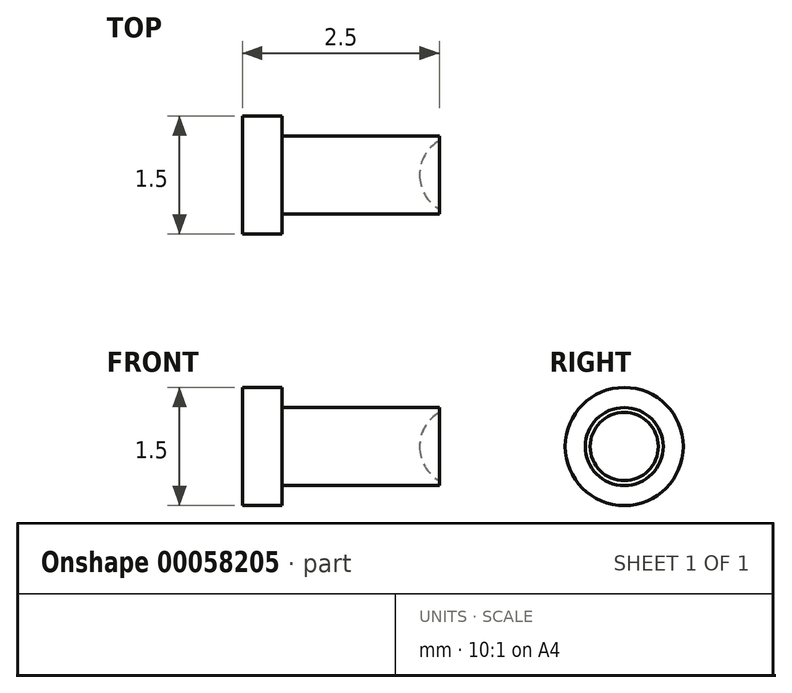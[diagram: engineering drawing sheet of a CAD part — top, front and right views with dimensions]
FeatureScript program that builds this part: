
annotation { "Feature Type Name" : "Feature", "Feature Type Description" : "" }
export const myFeature = defineFeature(function(context is Context, id is Id, definition is map)
    precondition{}
    {
        {
            var Q0;
            Q0=qCreatedBy(makeId("Front.planeOp"),FACE);
            var sketch = newSketch(context, id + "F0", { "sketchPlane" : qUnion([Q0])});
            skLineSegment(sketch, "E0", {"start": v(0, 0) * mm, "end": v(0, 0.75) * mm});
            skLineSegment(sketch, "E1", {"start": v(0, 0.75) * mm, "end": v(0.5, 0.75) * mm});
            skLineSegment(sketch, "E2", {"start": v(0.5, 0.75) * mm, "end": v(0.5, 0.5) * mm});
            skLineSegment(sketch, "E3", {"start": v(0.5, 0.5) * mm, "end": v(2.5, 0.5) * mm});
            skLineSegment(sketch, "E4", {"start": v(2.5, 0.5) * mm, "end": v(2.5, 0.43) * mm});
            skArc(sketch, "E5", {"start": v(2.5, 0.43) * mm, "mid": v(2.32, 0.25) * mm, "end": v(2.25, 0) * mm});
            skPoint(sketch, "E6.orphan", {"position": v(2.5, 0) * mm});
            skLineSegment(sketch, "E7", {"start": v(0, 0) * mm, "end": v(2.25, 0) * mm});
            skSolve(sketch);
        }
        {
            var Q0;
            Q0=qSketchRegion(id+"F0",true);
            var Q1;
            Q1=sQuery(id+"F0.wireOp",EDGE,"E7");
            revolve(context, id + "F1", {"entities" : qUnion([Q0]), "axis" : qUnion([Q1]), "revolveType" : RevolveType.FULL});
        }
    });
